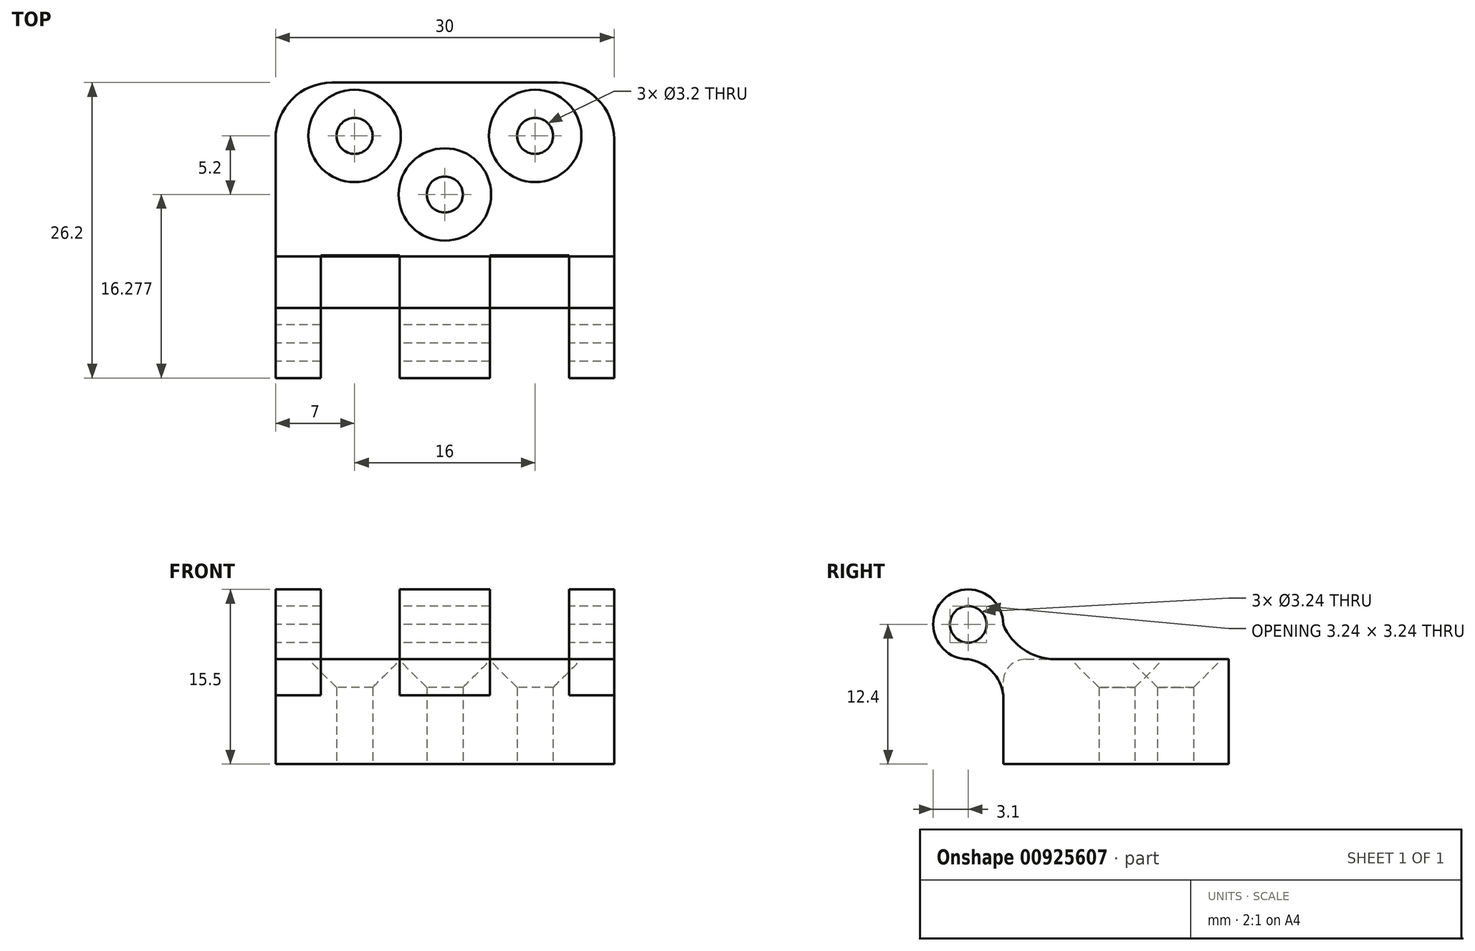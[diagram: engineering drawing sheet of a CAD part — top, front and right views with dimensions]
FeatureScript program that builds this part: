
annotation { "Feature Type Name" : "Feature", "Feature Type Description" : "" }
export const myFeature = defineFeature(function(context is Context, id is Id, definition is map)
    precondition{}
    {
        {
            var Q0;
            Q0=qCreatedBy(makeId("Top.planeOp"),FACE);
            var sketch = newSketch(context, id + "F0", { "sketchPlane" : qUnion([Q0])});
            skLineSegment(sketch, "E0.bottom", {"start": v(15, -10) * mm, "end": v(-15, -10) * mm});
            skLineSegment(sketch, "E0.top", {"start": v(15, 10) * mm, "end": v(-15, 10) * mm});
            skLineSegment(sketch, "E0.left", {"start": v(15, -10) * mm, "end": v(15, 10) * mm});
            skLineSegment(sketch, "E0.right", {"start": v(-15, -10) * mm, "end": v(-15, 10) * mm});
            skPoint(sketch, "E0.middle", {"position": v(0, 0) * mm});
            skCircle(sketch, "E1", {"center": v(-8, 5.28) * mm, "radius": 1.6 * mm});
            skCircle(sketch, "E2", {"center": v(8, 5.28) * mm, "radius": 1.6 * mm});
            skCircle(sketch, "E3", {"center": v(0, 0.08) * mm, "radius": 1.6 * mm});
            skLineSegment(sketch, "E4", {"start": v(0, 6.07) * mm, "end": v(0, -5.47) * mm, "construction": true});
            skLineSegment(sketch, "E5", {"start": v(-6.28, 0) * mm, "end": v(5.95, 0) * mm, "construction": true});
            skSolve(sketch);
        }
        {
            var Q0;
            Q0 = qSketchRegion(id + "F0", true);
            extrude(context, id + "F1", {"entities" : qUnion([Q0]), "depth" : 5 * mm, "offsetDistance" : 25 * mm});
        }
        {
            var Q0;
            Q0=makeQuery(id+"F1.opExtrude","SWEPT_FACE",FACE,{"disambiguationData":[OSD([sQuery(id+"F0.wireOp",EDGE,"E0.right")])]});
            var sketch = newSketch(context, id + "F2", { "sketchPlane" : qUnion([Q0])});
            skLineSegment(sketch, "E6.bottom", {"start": v(10, 5) * mm, "end": v(16.2, 5) * mm, "construction": true});
            skLineSegment(sketch, "E6.top", {"start": v(10, 11.2) * mm, "end": v(16.2, 11.2) * mm, "construction": true});
            skLineSegment(sketch, "E6.left", {"start": v(10, 5) * mm, "end": v(10, 11.2) * mm, "construction": true});
            skLineSegment(sketch, "E6.right", {"start": v(16.2, 5) * mm, "end": v(16.2, 11.2) * mm, "construction": true});
            skCircle(sketch, "E7", {"center": v(13.1, 8.1) * mm, "radius": 3.1 * mm});
            skPoint(sketch, "E7.centerSnap0", {"position": v(16.2, 8.1) * mm});
            skPoint(sketch, "E7.centerSnap1", {"position": v(13.1, 11.2) * mm});
            skArc(sketch, "E8", {"start": v(5.31, 5) * mm, "mid": v(8.13, 5.83) * mm, "end": v(10, 8.1) * mm});
            skPoint(sketch, "E8.first.point", {"position": v(5.31, 5) * mm});
            skPoint(sketch, "E8.second.point", {"position": v(10, 8.1) * mm});
            skPoint(sketch, "E8.third.point", {"position": v(5.43, 5) * mm});
            skArc(sketch, "E9", {"start": v(13.1, 5) * mm, "mid": v(11, 3.95) * mm, "end": v(10, 1.82) * mm});
            skPoint(sketch, "E9.first.point", {"position": v(10, 1.82) * mm});
            skPoint(sketch, "E9.second.point", {"position": v(13.1, 5) * mm});
            skPoint(sketch, "E9.third.point", {"position": v(10, 1.07) * mm});
            skSolve(sketch);
        }
        {
            var Q0;
            Q0 = qSketchRegion(id + "F2", true);
            var Q1;
            {var subQ0=sQuery(id+"F2.wireOp",EDGE,"E9");Q1=makeQuery(id+"F2.imprint","IMPRINT",FACE,{"disambiguationData":[TD([[makeQuery(id+"F2.imprint","IMPRINT",EDGE,{"derivedFrom":subQ0}),-1.0]])]});}
            var Q2;
            Q2=makeQuery(id+"F1.opExtrude","CAP_VERTEX",VERTEX,{"disambiguationData":[OSD([sQuery(id+"F0.wireOp",EDGE,"E0.bottom"),sQuery(id+"F0.wireOp",EDGE,"E0.left")])],"isStart":false});
            extrude(context, id + "F3", {"entities" : qUnion([Q0, Q1]), "operationType" : NewBodyOperationType.ADD, "endBound" : BoundingType.UP_TO_VERTEX, "oppositeDirection" : true, "depth" : 4 * mm, "endBoundEntityVertex" : qUnion([Q2]), "offsetDistance" : 25 * mm});
        }
        {
            var Q0;
            {var subQ0=sQuery(id+"F0.wireOp",EDGE,"E0.right");Q0=makeQuery(id+"F3.boolean.opBoolean","MERGE",FACE,{"derivedFrom":[makeQuery(id+"F1.opExtrude","SWEPT_FACE",FACE,{"disambiguationData":[OSD([subQ0])]}),makeQuery(id+"F3.opExtrude","CAP_FACE",FACE,{"disambiguationData":[OSD([sQuery(id+"F0.wireOp",EDGE,"E0.bottom"),subQ0,sQuery(id+"F2.wireOp",EDGE,"E7"),sQuery(id+"F2.wireOp",EDGE,"E8"),sQuery(id+"F2.wireOp",EDGE,"E9")])],"isStart":true})]});}
            cPlane(context, id + "F4", {"entities" : qUnion([Q0]), "cplaneType" : CPlaneType.OFFSET, "offset" : 4 * mm, "oppositeDirection" : true, "width" : 150 * mm, "height" : 150 * mm});
        }
        {
            var Q0;
            Q0=makeQuery(id+"F3.boolean.opBoolean","MERGE",FACE,{"derivedFrom":[makeQuery(id+"F1.opExtrude","SWEPT_FACE",FACE,{"disambiguationData":[OSD([sQuery(id+"F0.wireOp",EDGE,"E0.left")])]}),makeQuery(id+"F3.opExtrude","CAP_FACE",FACE,{"disambiguationData":[OSD([sQuery(id+"F0.wireOp",EDGE,"E0.bottom"),sQuery(id+"F0.wireOp",EDGE,"E0.right"),sQuery(id+"F2.wireOp",EDGE,"E7"),sQuery(id+"F2.wireOp",EDGE,"E8"),sQuery(id+"F2.wireOp",EDGE,"E9")])],"isStart":false})]});
            cPlane(context, id + "F5", {"entities" : qUnion([Q0]), "cplaneType" : CPlaneType.OFFSET, "offset" : 4 * mm, "oppositeDirection" : true, "width" : 150 * mm, "height" : 150 * mm});
        }
        {
            var Q0;
            Q0=qCreatedBy(id+"F5.planeOp",FACE);
            var sketch = newSketch(context, id + "F6", { "sketchPlane" : qUnion([Q0])});
            skPoint(sketch, "E10.MirrorP", {"position": v(-5.43, 5) * mm});
            skLineSegment(sketch, "E11.MirrorCS", {"start": v(-10, 5) * mm, "end": v(-16.2, 5) * mm, "construction": true});
            skCircle(sketch, "E12.MirrorC", {"center": v(-13.1, 8.1) * mm, "radius": 3.1 * mm});
            skPoint(sketch, "E13.MirrorP", {"position": v(-10, 8.1) * mm});
            skArc(sketch, "E14.MirrorCS", {"start": v(-13.1, 5) * mm, "mid": v(-11, 3.95) * mm, "end": v(-10, 1.82) * mm});
            skPoint(sketch, "E15.MirrorP", {"position": v(-5.31, 5) * mm});
            skArc(sketch, "E16.MirrorCS", {"start": v(-5.31, 5) * mm, "mid": v(-8.13, 5.83) * mm, "end": v(-10, 8.1) * mm});
            skPoint(sketch, "E17.MirrorP", {"position": v(-10, 1.82) * mm});
            skLineSegment(sketch, "E18.MirrorCS", {"start": v(-16.2, 5) * mm, "end": v(-16.2, 11.2) * mm, "construction": true});
            skPoint(sketch, "E19.MirrorP", {"position": v(-13.1, 5) * mm});
            skPoint(sketch, "E20.MirrorP", {"position": v(-13.1, 11.2) * mm});
            skLineSegment(sketch, "E21.MirrorCS", {"start": v(-10, 5) * mm, "end": v(-10, 11.2) * mm, "construction": true});
            skPoint(sketch, "E22.MirrorP", {"position": v(-16.2, 8.1) * mm});
            skLineSegment(sketch, "E23.MirrorCS", {"start": v(-10, 11.2) * mm, "end": v(-16.2, 11.2) * mm, "construction": true});
            skArc(sketch, "E24.0", {"start": v(-13.1, 5) * mm, "mid": v(-11, 3.95) * mm, "end": v(-10, 1.82) * mm, "construction": true});
            skLineSegment(sketch, "E25", {"start": v(-10, 1.82) * mm, "end": v(-10, 5) * mm});
            skLineSegment(sketch, "E26", {"start": v(-10, 5) * mm, "end": v(-5.31, 5) * mm});
            skSolve(sketch);
        }
        {
            var Q0;
            Q0 = qSketchRegion(id + "F6", true);
            extrude(context, id + "F7", {"entities" : qUnion([Q0]), "operationType" : NewBodyOperationType.REMOVE, "oppositeDirection" : true, "depth" : 7 * mm, "offsetDistance" : 25 * mm});
        }
        {
            var Q0;
            Q0=qCreatedBy(id+"F4.planeOp",FACE);
            var sketch = newSketch(context, id + "F8", { "sketchPlane" : qUnion([Q0])});
            skLineSegment(sketch, "E27.bottom", {"start": v(10, 5) * mm, "end": v(16.2, 5) * mm, "construction": true});
            skLineSegment(sketch, "E27.top", {"start": v(10, 11.2) * mm, "end": v(16.2, 11.2) * mm, "construction": true});
            skLineSegment(sketch, "E27.left", {"start": v(10, 5) * mm, "end": v(10, 11.2) * mm, "construction": true});
            skLineSegment(sketch, "E27.right", {"start": v(16.2, 5) * mm, "end": v(16.2, 11.2) * mm, "construction": true});
            skCircle(sketch, "E28", {"center": v(13.1, 8.1) * mm, "radius": 3.1 * mm});
            skPoint(sketch, "E28.centerSnap0", {"position": v(16.2, 8.1) * mm});
            skPoint(sketch, "E28.centerSnap1", {"position": v(13.1, 11.2) * mm});
            skArc(sketch, "E29", {"start": v(5.31, 5) * mm, "mid": v(8.13, 5.83) * mm, "end": v(10, 8.1) * mm});
            skPoint(sketch, "E29.first.point", {"position": v(5.31, 5) * mm});
            skPoint(sketch, "E29.second.point", {"position": v(10, 8.1) * mm});
            skPoint(sketch, "E29.third.point", {"position": v(5.43, 5) * mm});
            skArc(sketch, "E30", {"start": v(13.1, 5) * mm, "mid": v(11, 3.95) * mm, "end": v(10, 1.82) * mm});
            skPoint(sketch, "E30.first.point", {"position": v(10, 1.82) * mm});
            skPoint(sketch, "E30.second.point", {"position": v(13.1, 5) * mm});
            skArc(sketch, "E31.0", {"start": v(13.1, 5) * mm, "mid": v(11, 3.95) * mm, "end": v(10, 1.82) * mm, "construction": true});
            skLineSegment(sketch, "E32", {"start": v(10, 1.82) * mm, "end": v(10, 5) * mm});
            skLineSegment(sketch, "E33", {"start": v(10, 5) * mm, "end": v(5.31, 5) * mm});
            skSolve(sketch);
        }
        {
            var Q0;
            Q0 = qSketchRegion(id + "F8", true);
            extrude(context, id + "F9", {"entities" : qUnion([Q0]), "operationType" : NewBodyOperationType.REMOVE, "oppositeDirection" : true, "depth" : 7 * mm, "offsetDistance" : 25 * mm});
        }
        {
            var Q0;
            Q0=makeQuery(id+"F1.opExtrude","CAP_EDGE",EDGE,{"disambiguationData":[OSD([sQuery(id+"F0.wireOp",EDGE,"E1")])],"isStart":false});
            var Q1;
            Q1=makeQuery(id+"F1.opExtrude","CAP_EDGE",EDGE,{"disambiguationData":[OSD([sQuery(id+"F0.wireOp",EDGE,"E3")])],"isStart":false});
            var Q2;
            Q2=makeQuery(id+"F1.opExtrude","CAP_EDGE",EDGE,{"disambiguationData":[OSD([sQuery(id+"F0.wireOp",EDGE,"E2")])],"isStart":false});
            chamfer(context, id + "F10", {"entities" : qUnion([Q0, Q1, Q2]), "width" : 2.5 * mm, "tangentPropagation" : true});
        }
        {
            var Q0;
            Q0=makeQuery(id+"F1.opExtrude","SWEPT_EDGE",EDGE,{"disambiguationData":[OSD([sQuery(id+"F0.wireOp",EDGE,"E0.top"),sQuery(id+"F0.wireOp",EDGE,"E0.right")])]});
            var Q1;
            Q1=makeQuery(id+"F1.opExtrude","SWEPT_EDGE",EDGE,{"disambiguationData":[OSD([sQuery(id+"F0.wireOp",EDGE,"E0.top"),sQuery(id+"F0.wireOp",EDGE,"E0.left")])]});
            fillet(context, id + "F11", {"entities" : qUnion([Q0, Q1]), "radius" : 5 * mm, "tangentPropagation" : true, "allowEdgeOverflow" : false});
        }
        {
            var Q0;
            {var subQ0=sQuery(id+"F0.wireOp",EDGE,"E0.right");Q0=makeQuery(id+"F3.boolean.opBoolean","MERGE",FACE,{"derivedFrom":[makeQuery(id+"F1.opExtrude","SWEPT_FACE",FACE,{"disambiguationData":[OSD([subQ0])]}),makeQuery(id+"F3.opExtrude","CAP_FACE",FACE,{"disambiguationData":[OSD([sQuery(id+"F0.wireOp",EDGE,"E0.bottom"),subQ0,sQuery(id+"F2.wireOp",EDGE,"E7"),sQuery(id+"F2.wireOp",EDGE,"E8"),sQuery(id+"F2.wireOp",EDGE,"E9")])],"isStart":true})]});}
            var sketch = newSketch(context, id + "F12", { "sketchPlane" : qUnion([Q0])});
            skArc(sketch, "E34.0", {"start": v(13.1, 5) * mm, "mid": v(15.3, 10.3) * mm, "end": v(10, 8.1) * mm, "construction": true});
            skCircle(sketch, "E35", {"center": v(13.1, 8.1) * mm, "radius": 1.62 * mm});
            skSolve(sketch);
        }
        {
            var Q0;
            Q0=makeQuery(id+"F12.imprint","IMPRINT",FACE,{"disambiguationData":[TD([[makeQuery(id+"F12.imprint","IMPRINT",EDGE,{"derivedFrom":sQuery(id+"F12.wireOp",EDGE,"E35")}),1.0]])]});
            extrude(context, id + "F13", {"entities" : qUnion([Q0]), "operationType" : NewBodyOperationType.REMOVE, "endBound" : BoundingType.THROUGH_ALL, "oppositeDirection" : true, "depth" : 25 * mm, "offsetDistance" : 25 * mm});
        }
        {
            var Q0;
            Q0=makeQuery(id+"F9.boolean.opBoolean","COPY",EDGE,{"derivedFrom":makeQuery(id+"F9.opExtrude","SWEPT_EDGE",EDGE,{"disambiguationData":[OSD([sQuery(id+"F8.wireOp",EDGE,"E32"),sQuery(id+"F8.wireOp",EDGE,"E33")])]})});
            var Q1;
            Q1=makeQuery(id+"F7.boolean.opBoolean","COPY",EDGE,{"derivedFrom":makeQuery(id+"F7.opExtrude","SWEPT_EDGE",EDGE,{"disambiguationData":[OSD([sQuery(id+"F6.wireOp",EDGE,"E25"),sQuery(id+"F6.wireOp",EDGE,"E26")])]})});
            fillet(context, id + "F14", {"entities" : qUnion([Q0, Q1]), "radius" : 2 * mm, "tangentPropagation" : true, "allowEdgeOverflow" : false});
        }
        {
            var Q0;
            Q0=makeQuery(id+"F1.opExtrude","CAP_FACE",FACE,{"disambiguationData":[OSD([sQuery(id+"F0.wireOp",EDGE,"E0.bottom"),sQuery(id+"F0.wireOp",EDGE,"E0.top"),sQuery(id+"F0.wireOp",EDGE,"E0.left"),sQuery(id+"F0.wireOp",EDGE,"E0.right"),sQuery(id+"F0.wireOp",EDGE,"E1"),sQuery(id+"F0.wireOp",EDGE,"E2"),sQuery(id+"F0.wireOp",EDGE,"E3")])],"isStart":true});
            extrude(context, id + "F15", {"entities" : qUnion([Q0]), "operationType" : NewBodyOperationType.ADD, "depth" : 4.3 * mm, "offsetDistance" : 25 * mm});
        }
    });
